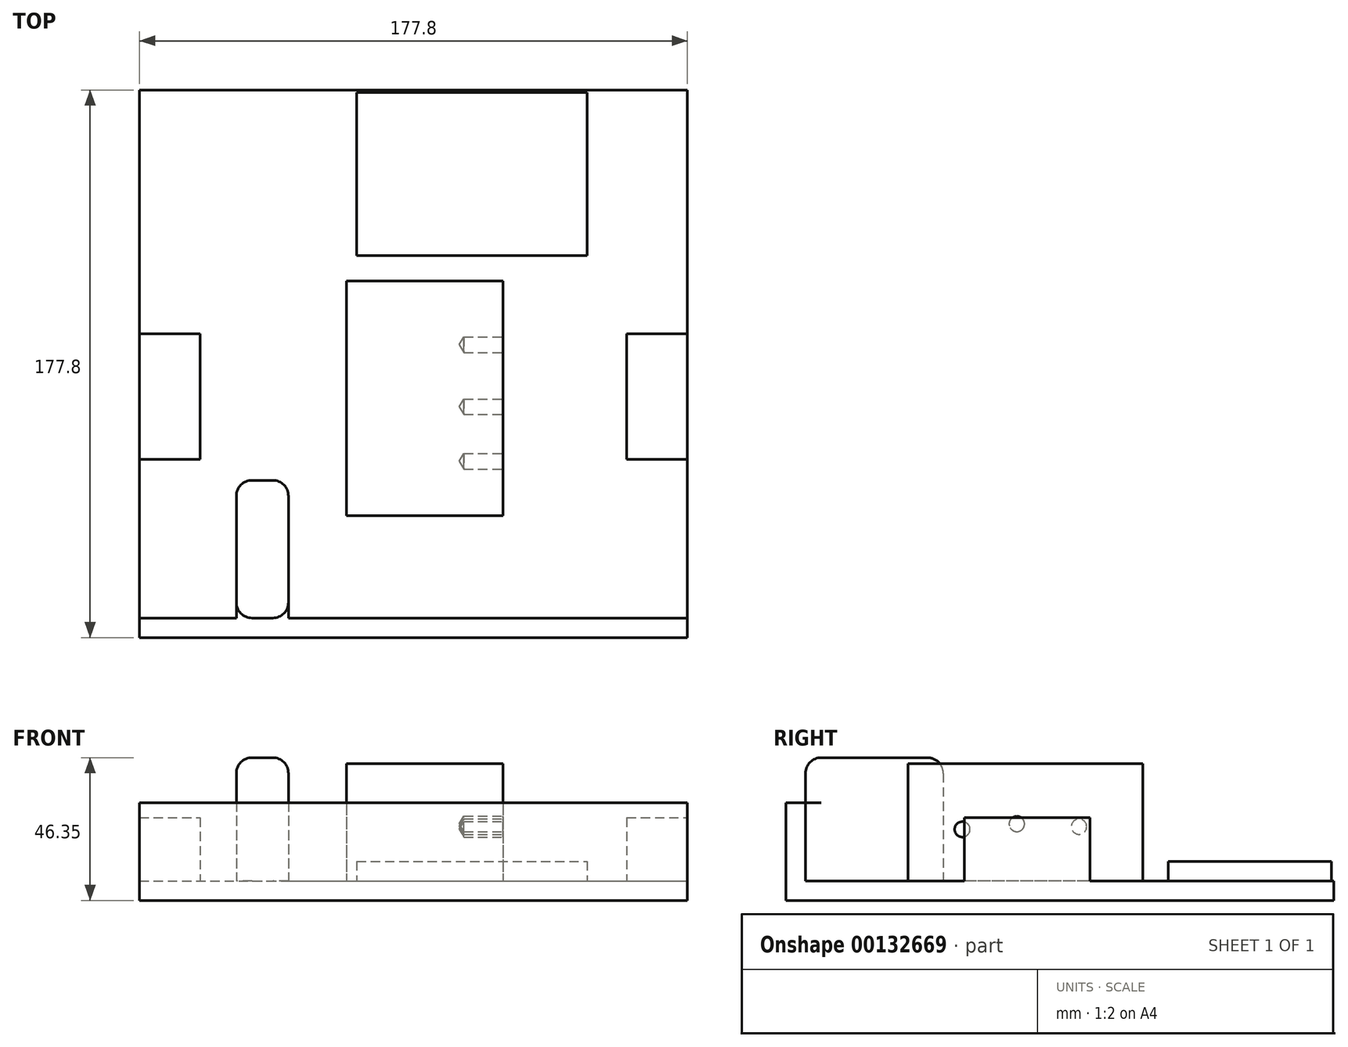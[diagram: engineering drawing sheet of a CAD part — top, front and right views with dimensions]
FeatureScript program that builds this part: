
annotation { "Feature Type Name" : "Feature", "Feature Type Description" : "" }
export const myFeature = defineFeature(function(context is Context, id is Id, definition is map)
    precondition{}
    {
        {
            var Q0;
            Q0=qCreatedBy(makeId("Top.planeOp"),FACE);
            var sketch = newSketch(context, id + "F0", { "sketchPlane" : qUnion([Q0])});
            skLineSegment(sketch, "E0.bottom", {"start": v(-117.97, 61.97) * mm, "end": v(59.83, 61.97) * mm});
            skLineSegment(sketch, "E0.top", {"start": v(-117.97, -115.83) * mm, "end": v(59.83, -115.83) * mm});
            skLineSegment(sketch, "E0.left", {"start": v(-117.97, 61.97) * mm, "end": v(-117.97, -115.83) * mm});
            skLineSegment(sketch, "E0.right", {"start": v(59.83, 61.97) * mm, "end": v(59.83, -115.83) * mm});
            skSolve(sketch);
        }
        {
            var Q0;
            Q0=makeQuery(id+"F0.imprint","IMPRINT",FACE,{"disambiguationData":[TD([[makeQuery(id+"F0.imprint","IMPRINT",EDGE,{"derivedFrom":sQuery(id+"F0.wireOp",EDGE,"E0.bottom")}),-1.0]])]});
            extrude(context, id + "F1", {"entities" : qUnion([Q0]), "depth" : 6.35 * mm});
        }
        {
            var Q0;
            Q0=makeQuery(id+"F1.opExtrude","CAP_FACE",FACE,{"disambiguationData":[OSD([sQuery(id+"F0.wireOp",EDGE,"E0.bottom"),sQuery(id+"F0.wireOp",EDGE,"E0.top"),sQuery(id+"F0.wireOp",EDGE,"E0.left"),sQuery(id+"F0.wireOp",EDGE,"E0.right")])],"isStart":false});
            var sketch = newSketch(context, id + "F2", { "sketchPlane" : qUnion([Q0])});
            skLineSegment(sketch, "E1.bottom", {"start": v(40.13, -17.23) * mm, "end": v(59.83, -17.23) * mm});
            skLineSegment(sketch, "E1.top", {"start": v(40.13, -57.93) * mm, "end": v(59.83, -57.93) * mm});
            skLineSegment(sketch, "E1.left", {"start": v(40.13, -17.23) * mm, "end": v(40.13, -57.93) * mm});
            skLineSegment(sketch, "E1.right", {"start": v(59.83, -17.23) * mm, "end": v(59.83, -57.93) * mm});
            skLineSegment(sketch, "E2.bottom", {"start": v(-117.97, -17.23) * mm, "end": v(-98.27, -17.23) * mm});
            skLineSegment(sketch, "E2.top", {"start": v(-117.97, -57.93) * mm, "end": v(-98.27, -57.93) * mm});
            skLineSegment(sketch, "E2.left", {"start": v(-117.97, -17.23) * mm, "end": v(-117.97, -57.93) * mm});
            skLineSegment(sketch, "E2.right", {"start": v(-98.27, -17.23) * mm, "end": v(-98.27, -57.93) * mm});
            skSolve(sketch);
        }
        {
            var Q0;
            Q0 = qSketchRegion(id + "F2", true);
            extrude(context, id + "F3", {"entities" : qUnion([Q0]), "operationType" : NewBodyOperationType.ADD, "depth" : 20.5 * mm});
        }
        {
            var Q0;
            Q0=makeQuery(id+"F1.opExtrude","CAP_FACE",FACE,{"disambiguationData":[OSD([sQuery(id+"F0.wireOp",EDGE,"E0.bottom"),sQuery(id+"F0.wireOp",EDGE,"E0.top"),sQuery(id+"F0.wireOp",EDGE,"E0.left"),sQuery(id+"F0.wireOp",EDGE,"E0.right")])],"isStart":false});
            var sketch = newSketch(context, id + "F4", { "sketchPlane" : qUnion([Q0])});
            skLineSegment(sketch, "E3.bottom", {"start": v(-50.8, 0) * mm, "end": v(0, 0) * mm});
            skLineSegment(sketch, "E3.top", {"start": v(-50.8, -76.2) * mm, "end": v(0, -76.2) * mm});
            skLineSegment(sketch, "E3.left", {"start": v(-50.8, 0) * mm, "end": v(-50.8, -76.2) * mm});
            skLineSegment(sketch, "E3.right", {"start": v(0, 0) * mm, "end": v(0, -76.2) * mm});
            skSolve(sketch);
        }
        {
            var Q0;
            Q0=makeQuery(id+"F4.imprint","IMPRINT",FACE,{"disambiguationData":[TD([[makeQuery(id+"F4.imprint","IMPRINT",EDGE,{"derivedFrom":sQuery(id+"F4.wireOp",EDGE,"E3.bottom")}),-1.0]])]});
            extrude(context, id + "F5", {"entities" : qUnion([Q0]), "operationType" : NewBodyOperationType.ADD, "depth" : 38.1 * mm});
        }
        {
            var Q0;
            Q0=makeQuery(id+"F1.opExtrude","CAP_FACE",FACE,{"disambiguationData":[OSD([sQuery(id+"F0.wireOp",EDGE,"E0.bottom"),sQuery(id+"F0.wireOp",EDGE,"E0.top"),sQuery(id+"F0.wireOp",EDGE,"E0.left"),sQuery(id+"F0.wireOp",EDGE,"E0.right")])],"isStart":false});
            var sketch = newSketch(context, id + "F6", { "sketchPlane" : qUnion([Q0])});
            skLineSegment(sketch, "E4.bottom", {"start": v(-47.49, 61.21) * mm, "end": v(27.31, 61.21) * mm});
            skLineSegment(sketch, "E4.top", {"start": v(-47.49, 8.21) * mm, "end": v(27.31, 8.21) * mm});
            skLineSegment(sketch, "E4.left", {"start": v(-47.49, 61.21) * mm, "end": v(-47.49, 8.21) * mm});
            skLineSegment(sketch, "E4.right", {"start": v(27.31, 61.21) * mm, "end": v(27.31, 8.21) * mm});
            skSolve(sketch);
        }
        {
            var Q0;
            Q0=makeQuery(id+"F6.imprint","IMPRINT",FACE,{"disambiguationData":[TD([[makeQuery(id+"F6.imprint","IMPRINT",EDGE,{"derivedFrom":sQuery(id+"F6.wireOp",EDGE,"E4.bottom")}),-1.0]])]});
            extrude(context, id + "F7", {"entities" : qUnion([Q0]), "operationType" : NewBodyOperationType.ADD, "depth" : 6.35 * mm});
        }
        {
            var Q0;
            Q0=makeQuery(id+"F1.opExtrude","CAP_FACE",FACE,{"disambiguationData":[OSD([sQuery(id+"F0.wireOp",EDGE,"E0.bottom"),sQuery(id+"F0.wireOp",EDGE,"E0.top"),sQuery(id+"F0.wireOp",EDGE,"E0.left"),sQuery(id+"F0.wireOp",EDGE,"E0.right")])],"isStart":false});
            var sketch = newSketch(context, id + "F8", { "sketchPlane" : qUnion([Q0])});
            skLineSegment(sketch, "E5.bottom", {"start": v(-117.97, -109.48) * mm, "end": v(59.83, -109.48) * mm});
            skLineSegment(sketch, "E5.top", {"start": v(-117.97, -115.83) * mm, "end": v(59.83, -115.83) * mm});
            skLineSegment(sketch, "E5.left", {"start": v(-117.97, -109.48) * mm, "end": v(-117.97, -115.83) * mm});
            skLineSegment(sketch, "E5.right", {"start": v(59.83, -109.48) * mm, "end": v(59.83, -115.83) * mm});
            skSolve(sketch);
        }
        {
            var Q0;
            Q0 = qSketchRegion(id + "F8", true);
            extrude(context, id + "F9", {"entities" : qUnion([Q0]), "operationType" : NewBodyOperationType.ADD, "depth" : 25.4 * mm});
        }
        {
            var Q0;
            Q0=makeQuery(id+"F1.opExtrude","CAP_FACE",FACE,{"disambiguationData":[OSD([sQuery(id+"F0.wireOp",EDGE,"E0.bottom"),sQuery(id+"F0.wireOp",EDGE,"E0.top"),sQuery(id+"F0.wireOp",EDGE,"E0.left"),sQuery(id+"F0.wireOp",EDGE,"E0.right")])],"isStart":false});
            var sketch = newSketch(context, id + "F10", { "sketchPlane" : qUnion([Q0])});
            skLineSegment(sketch, "E6.bottom", {"start": v(-86.56, -109.48) * mm, "end": v(-69.66, -109.48) * mm});
            skLineSegment(sketch, "E6.top", {"start": v(-86.56, -64.78) * mm, "end": v(-69.66, -64.78) * mm});
            skLineSegment(sketch, "E6.left", {"start": v(-86.56, -109.48) * mm, "end": v(-86.56, -64.78) * mm});
            skLineSegment(sketch, "E6.right", {"start": v(-69.66, -109.48) * mm, "end": v(-69.66, -64.78) * mm});
            skSolve(sketch);
        }
        {
            var Q0;
            Q0=makeQuery(id+"F10.imprint","IMPRINT",FACE,{"disambiguationData":[TD([[makeQuery(id+"F10.imprint","IMPRINT",EDGE,{"derivedFrom":sQuery(id+"F10.wireOp",EDGE,"E6.bottom")}),1.0]])]});
            extrude(context, id + "F11", {"entities" : qUnion([Q0]), "operationType" : NewBodyOperationType.ADD, "depth" : 40 * mm});
        }
        {
            var Q0;
            Q0=makeQuery(id+"F5.opExtrude","SWEPT_FACE",FACE,{"disambiguationData":[OSD([sQuery(id+"F4.wireOp",EDGE,"E3.right")])]});
            var sketch = newSketch(context, id + "F12", { "sketchPlane" : qUnion([Q0])});
            skCircle(sketch, "E7", {"center": v(-58.6, 23.07) * mm, "radius": 3.57 * mm});
            skCircle(sketch, "E8", {"center": v(-40.92, 24.82) * mm, "radius": 3.55 * mm});
            skCircle(sketch, "E9", {"center": v(-20.75, 23.94) * mm, "radius": 4.06 * mm});
            skSolve(sketch);
        }
        {
            var Q0;
            Q0=sQuery(id+"F12.wireOp",VERTEX,"E7.center");
            var Q1;
            Q1=sQuery(id+"F12.wireOp",VERTEX,"E8.center");
            var Q2;
            Q2=sQuery(id+"F12.wireOp",VERTEX,"E9.center");
            var Q3;
            Q3=makeQuery(id+"F1.opExtrude","SWEPT_BODY",BODY,{"disambiguationData":[OSD([sQuery(id+"F0.wireOp",EDGE,"E0.bottom"),sQuery(id+"F0.wireOp",EDGE,"E0.top"),sQuery(id+"F0.wireOp",EDGE,"E0.left"),sQuery(id+"F0.wireOp",EDGE,"E0.right")])]});
            hole(context, id + "F13", {"style" : HoleStyle.SIMPLE, "endStyle" : HoleEndStyle.BLIND, "holeDiameter" : 5 * mm, "holeDepth" : 12.7 * mm, "locations" : qUnion([Q0, Q1, Q2]), "scope" : qUnion([Q3])});
        }
        {
            var Q0;
            Q0=makeQuery(id+"F11.opExtrude","CAP_EDGE",EDGE,{"disambiguationData":[OSD([sQuery(id+"F10.wireOp",EDGE,"E6.right")])],"isStart":false});
            var Q1;
            Q1=makeQuery(id+"F11.opExtrude","CAP_EDGE",EDGE,{"disambiguationData":[OSD([sQuery(id+"F10.wireOp",EDGE,"E6.top")])],"isStart":false});
            var Q2;
            Q2=makeQuery(id+"F11.opExtrude","CAP_EDGE",EDGE,{"disambiguationData":[OSD([sQuery(id+"F10.wireOp",EDGE,"E6.left")])],"isStart":false});
            var Q3;
            Q3=makeQuery(id+"F11.opExtrude","CAP_EDGE",EDGE,{"disambiguationData":[OSD([sQuery(id+"F10.wireOp",EDGE,"E6.bottom")])],"isStart":false});
            var Q4;
            Q4=makeQuery(id+"F11.opExtrude","SWEPT_EDGE",EDGE,{"disambiguationData":[OSD([sQuery(id+"F10.wireOp",EDGE,"E6.top"),sQuery(id+"F10.wireOp",EDGE,"E6.left")])]});
            var Q5;
            Q5=makeQuery(id+"F11.opExtrude","SWEPT_EDGE",EDGE,{"disambiguationData":[OSD([sQuery(id+"F10.wireOp",EDGE,"E6.top"),sQuery(id+"F10.wireOp",EDGE,"E6.right")])]});
            var Q6;
            {var subQ0=sQuery(id+"F10.wireOp",EDGE,"E6.bottom");var subQ1=sQuery(id+"F10.wireOp",EDGE,"E6.right");Q6=makeQuery(id+"F11.boolean.opBoolean","SPLIT",EDGE,{"disambiguationData":[topologyDisambiguationEdgeConnected([makeQuery(id+"F11.opExtrude","SWEPT_FACE",FACE,{"disambiguationData":[OSD([subQ0])]})])],"derivedFrom":makeQuery(id+"F11.opExtrude","SWEPT_EDGE",EDGE,{"disambiguationData":[OSD([sQuery(id+"F8.wireOp",EDGE,"E5.bottom"),subQ0,subQ1])]})});}
            fillet(context, id + "F14", {"entities" : qUnion([Q0, Q1, Q2, Q3, Q4, Q5, Q6]), "radius" : 5.08 * mm, "tangentPropagation" : true, "allowEdgeOverflow" : false});
        }
        {
            var Q0;
            {var subQ0=sQuery(id+"F10.wireOp",EDGE,"E6.bottom");var subQ1=sQuery(id+"F10.wireOp",EDGE,"E6.left");Q0=makeQuery(id+"F11.boolean.opBoolean","SPLIT",EDGE,{"disambiguationData":[topologyDisambiguationEdgeConnected([makeQuery(id+"F11.opExtrude","SWEPT_FACE",FACE,{"disambiguationData":[OSD([subQ0])]})])],"derivedFrom":makeQuery(id+"F11.opExtrude","SWEPT_EDGE",EDGE,{"disambiguationData":[OSD([sQuery(id+"F8.wireOp",EDGE,"E5.bottom"),subQ0,subQ1])]})});}
            fillet(context, id + "F15", {"entities" : qUnion([Q0]), "radius" : 5.08 * mm, "tangentPropagation" : true, "allowEdgeOverflow" : false});
        }
    });
